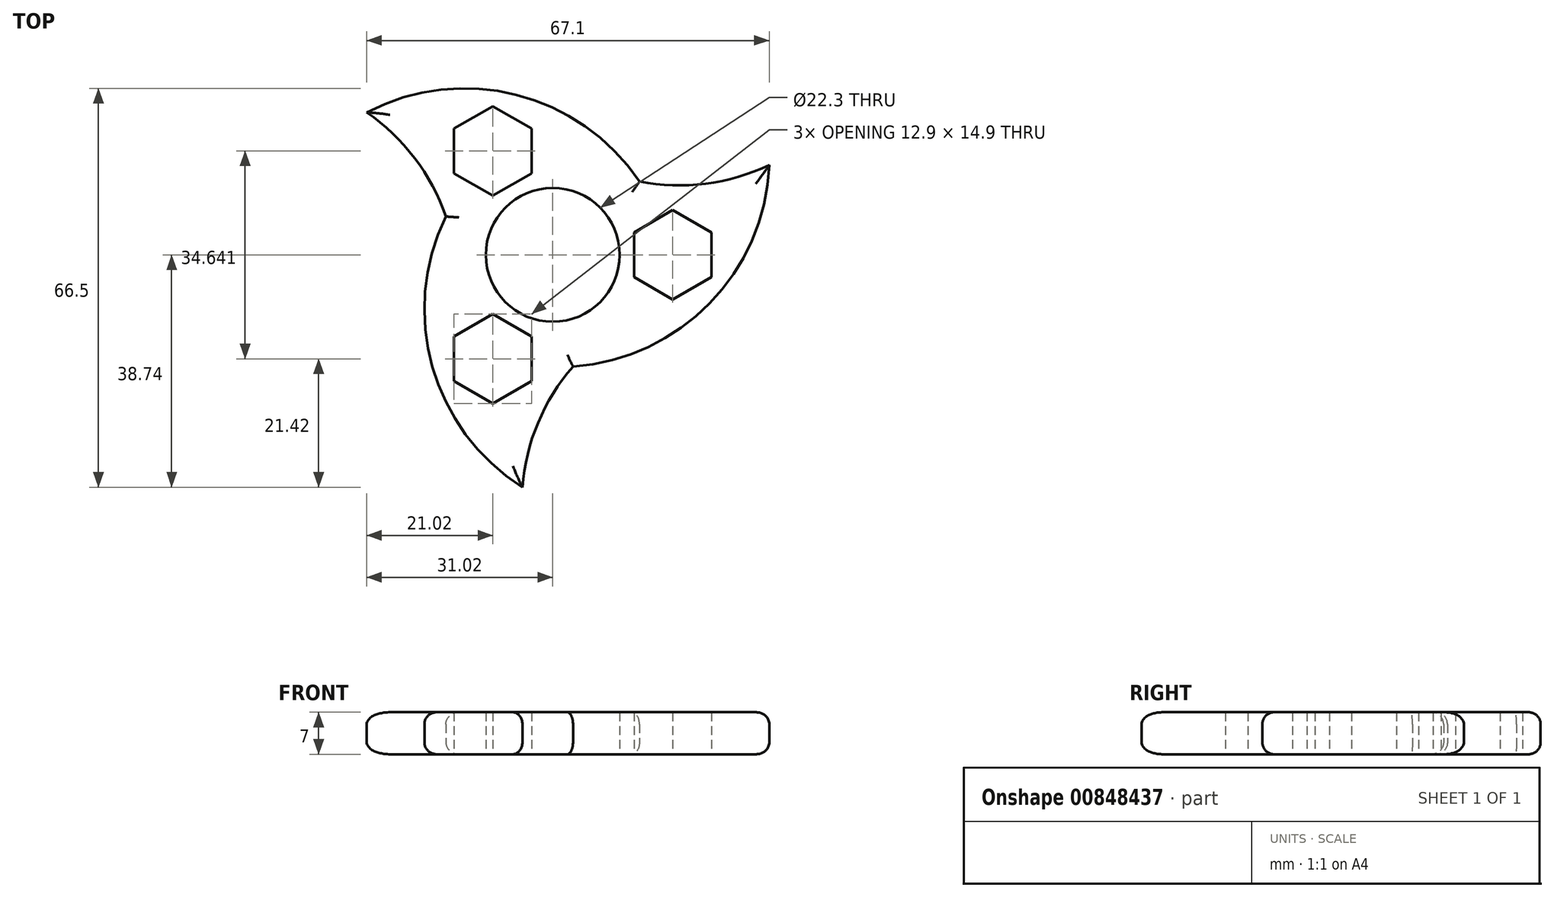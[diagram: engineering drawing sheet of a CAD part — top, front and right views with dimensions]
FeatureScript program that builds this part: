
annotation { "Feature Type Name" : "Feature", "Feature Type Description" : "" }
export const myFeature = defineFeature(function(context is Context, id is Id, definition is map)
    precondition{}
    {
        {
            var Q0;
            Q0=qCreatedBy(makeId("Top.planeOp"),FACE);
            var sketch = newSketch(context, id + "F0", { "sketchPlane" : qUnion([Q0])});
            skCircle(sketch, "E0", {"center": v(0, 0) * mm, "radius": 11.15 * mm});
            skCircle(sketch, "E1.cCircle", {"center": v(20, 0) * mm, "radius": 6.45 * mm, "construction": true});
            skLineSegment(sketch, "E1.0", {"start": v(26.45, 3.72) * mm, "end": v(26.45, -3.72) * mm});
            skLineSegment(sketch, "E1.1", {"start": v(26.45, -3.72) * mm, "end": v(20, -7.45) * mm});
            skLineSegment(sketch, "E1.2", {"start": v(20, -7.45) * mm, "end": v(13.55, -3.72) * mm});
            skLineSegment(sketch, "E1.3", {"start": v(13.55, -3.72) * mm, "end": v(13.55, 3.72) * mm});
            skLineSegment(sketch, "E1.4", {"start": v(13.55, 3.72) * mm, "end": v(20, 7.45) * mm});
            skLineSegment(sketch, "E1.5", {"start": v(20, 7.45) * mm, "end": v(26.45, 3.72) * mm});
            skPoint(sketch, "E1.0.midPoint", {"position": v(26.45, 0) * mm});
            skPoint(sketch, "E2", {"position": v(0, 18.7) * mm});
            skPoint(sketch, "E3.MirrorP", {"position": v(0, -18.7) * mm});
            skArc(sketch, "E4", {"start": v(0, 18.7) * mm, "mid": v(17.52, 11.78) * mm, "end": v(36.08, 14.98) * mm});
            skArc(sketch, "E5", {"start": v(0, -18.7) * mm, "mid": v(24.95, -9.25) * mm, "end": v(36.08, 14.98) * mm});
            skArc(sketch, "E6.1.0", {"start": v(-16.19, -9.35) * mm, "mid": v(-18.96, 9.29) * mm, "end": v(-31.02, 23.76) * mm});
            skArc(sketch, "E6.1.1", {"start": v(16.19, 9.35) * mm, "mid": v(-4.46, 26.23) * mm, "end": v(-31.02, 23.76) * mm});
            skArc(sketch, "E6.2.0", {"start": v(16.19, -9.35) * mm, "mid": v(1.44, -21.06) * mm, "end": v(-5.07, -38.74) * mm});
            skArc(sketch, "E6.2.1", {"start": v(-16.19, 9.35) * mm, "mid": v(-20.49, -16.98) * mm, "end": v(-5.07, -38.74) * mm});
            skLineSegment(sketch, "E7.1.0", {"start": v(-10, 9.87) * mm, "end": v(-16.45, 13.6) * mm});
            skLineSegment(sketch, "E7.1.1", {"start": v(-16.45, 13.6) * mm, "end": v(-16.45, 21.04) * mm});
            skLineSegment(sketch, "E7.1.2", {"start": v(-16.45, 21.04) * mm, "end": v(-10, 24.77) * mm});
            skLineSegment(sketch, "E7.1.3", {"start": v(-10, 24.77) * mm, "end": v(-3.55, 21.04) * mm});
            skLineSegment(sketch, "E7.1.4", {"start": v(-3.55, 21.04) * mm, "end": v(-3.55, 13.6) * mm});
            skLineSegment(sketch, "E7.1.5", {"start": v(-3.55, 13.6) * mm, "end": v(-10, 9.87) * mm});
            skLineSegment(sketch, "E7.2.0", {"start": v(-3.55, -13.6) * mm, "end": v(-3.55, -21.04) * mm});
            skLineSegment(sketch, "E7.2.1", {"start": v(-3.55, -21.04) * mm, "end": v(-10, -24.77) * mm});
            skLineSegment(sketch, "E7.2.2", {"start": v(-10, -24.77) * mm, "end": v(-16.45, -21.04) * mm});
            skLineSegment(sketch, "E7.2.3", {"start": v(-16.45, -21.04) * mm, "end": v(-16.45, -13.6) * mm});
            skLineSegment(sketch, "E7.2.4", {"start": v(-16.45, -13.6) * mm, "end": v(-10, -9.87) * mm});
            skLineSegment(sketch, "E7.2.5", {"start": v(-10, -9.87) * mm, "end": v(-3.55, -13.6) * mm});
            skSolve(sketch);
        }
        {
            var Q0;
            Q0=makeQuery(id+"F0.imprint","IMPRINT",FACE,{"disambiguationData":[TD([[makeQuery(id+"F0.imprint","IMPRINT",EDGE,{"derivedFrom":sQuery(id+"F0.wireOp",EDGE,"E0")}),-1.0]])]});
            extrude(context, id + "F1", {"entities" : qUnion([Q0]), "depth" : 7 * mm, "offsetDistance" : 25 * mm});
        }
        {
            var Q0;
            Q0=makeQuery(id+"F1.opExtrude","CAP_EDGE",EDGE,{"disambiguationData":[OSD([sQuery(id+"F0.wireOp",EDGE,"E6.1.0")])],"isStart":false});
            var Q1;
            Q1=makeQuery(id+"F1.opExtrude","CAP_EDGE",EDGE,{"disambiguationData":[OSD([sQuery(id+"F0.wireOp",EDGE,"E6.2.1")])],"isStart":false});
            var Q2;
            Q2=makeQuery(id+"F1.opExtrude","CAP_EDGE",EDGE,{"disambiguationData":[OSD([sQuery(id+"F0.wireOp",EDGE,"E6.2.0")])],"isStart":false});
            var Q3;
            Q3=makeQuery(id+"F1.opExtrude","CAP_EDGE",EDGE,{"disambiguationData":[OSD([sQuery(id+"F0.wireOp",EDGE,"E5")])],"isStart":false});
            var Q4;
            Q4=makeQuery(id+"F1.opExtrude","CAP_EDGE",EDGE,{"disambiguationData":[OSD([sQuery(id+"F0.wireOp",EDGE,"E4")])],"isStart":false});
            var Q5;
            Q5=makeQuery(id+"F1.opExtrude","CAP_EDGE",EDGE,{"disambiguationData":[OSD([sQuery(id+"F0.wireOp",EDGE,"E6.1.1")])],"isStart":false});
            var Q6;
            Q6=makeQuery(id+"F1.opExtrude","CAP_EDGE",EDGE,{"disambiguationData":[OSD([sQuery(id+"F0.wireOp",EDGE,"E6.1.1")])],"isStart":true});
            var Q7;
            Q7=makeQuery(id+"F1.opExtrude","CAP_EDGE",EDGE,{"disambiguationData":[OSD([sQuery(id+"F0.wireOp",EDGE,"E6.1.0")])],"isStart":true});
            var Q8;
            Q8=makeQuery(id+"F1.opExtrude","CAP_EDGE",EDGE,{"disambiguationData":[OSD([sQuery(id+"F0.wireOp",EDGE,"E6.2.1")])],"isStart":true});
            var Q9;
            Q9=makeQuery(id+"F1.opExtrude","CAP_EDGE",EDGE,{"disambiguationData":[OSD([sQuery(id+"F0.wireOp",EDGE,"E6.2.0")])],"isStart":true});
            var Q10;
            Q10=makeQuery(id+"F1.opExtrude","CAP_EDGE",EDGE,{"disambiguationData":[OSD([sQuery(id+"F0.wireOp",EDGE,"E5")])],"isStart":true});
            var Q11;
            Q11=makeQuery(id+"F1.opExtrude","CAP_EDGE",EDGE,{"disambiguationData":[OSD([sQuery(id+"F0.wireOp",EDGE,"E4")])],"isStart":true});
            fillet(context, id + "F2", {"entities" : qUnion([Q0, Q1, Q2, Q3, Q4, Q5, Q6, Q7, Q8, Q9, Q10, Q11]), "radius" : 2 * mm, "tangentPropagation" : true, "allowEdgeOverflow" : false});
        }
    });
